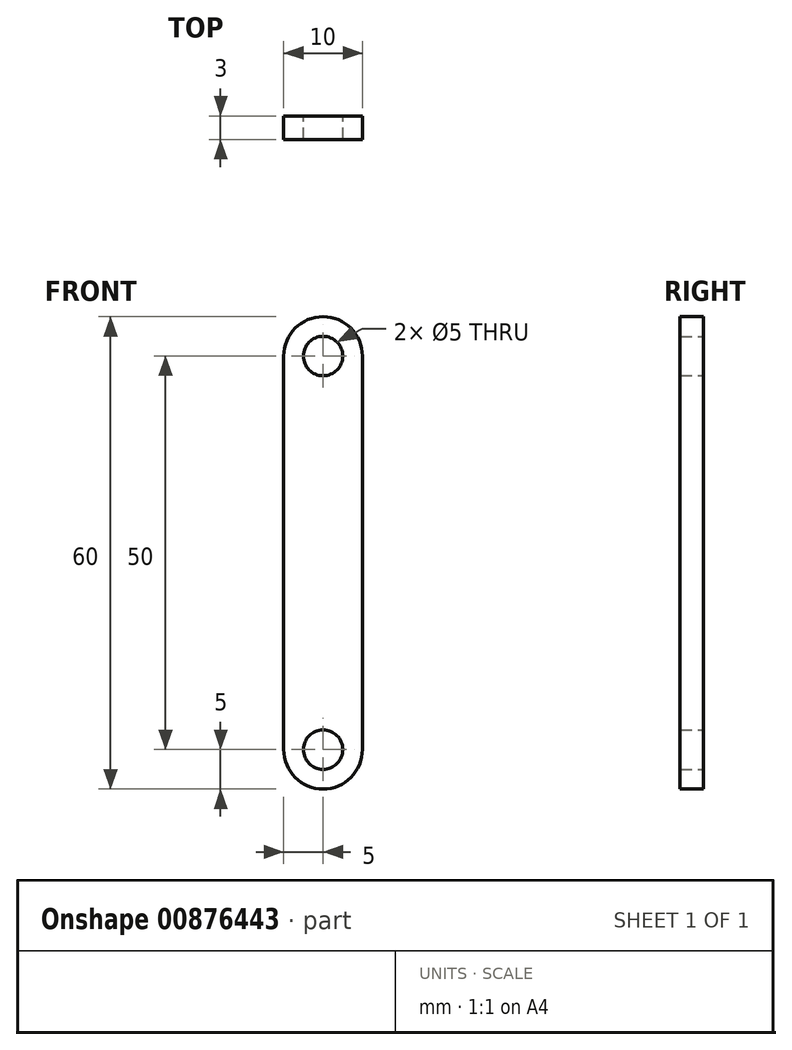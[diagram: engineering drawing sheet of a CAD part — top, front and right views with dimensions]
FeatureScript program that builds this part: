
annotation { "Feature Type Name" : "Feature", "Feature Type Description" : "" }
export const myFeature = defineFeature(function(context is Context, id is Id, definition is map)
    precondition{}
    {
        {
            var Q0;
            Q0=qCreatedBy(makeId("Front.planeOp"),FACE);
            var sketch = newSketch(context, id + "F0", { "sketchPlane" : qUnion([Q0])});
            skLineSegment(sketch, "E0.left", {"start": v(5, 25) * mm, "end": v(5, -25) * mm});
            skLineSegment(sketch, "E0.right", {"start": v(-5, 25) * mm, "end": v(-5, -25) * mm});
            skPoint(sketch, "E0.middle", {"position": v(0, 0) * mm});
            skArc(sketch, "E1", {"start": v(5, 25) * mm, "mid": v(0, 30) * mm, "end": v(-5, 25) * mm});
            skArc(sketch, "E2", {"start": v(-5, -25) * mm, "mid": v(0, -30) * mm, "end": v(5, -25) * mm});
            skCircle(sketch, "E3", {"center": v(0, 25) * mm, "radius": 2.5 * mm});
            skCircle(sketch, "E4", {"center": v(0, -25) * mm, "radius": 2.5 * mm});
            skSolve(sketch);
        }
        {
            var Q0;
            Q0 = qSketchRegion(id + "F0", true);
            extrude(context, id + "F1", {"entities" : qUnion([Q0]), "depth" : 3 * mm, "offsetDistance" : 25 * mm});
        }
    });
